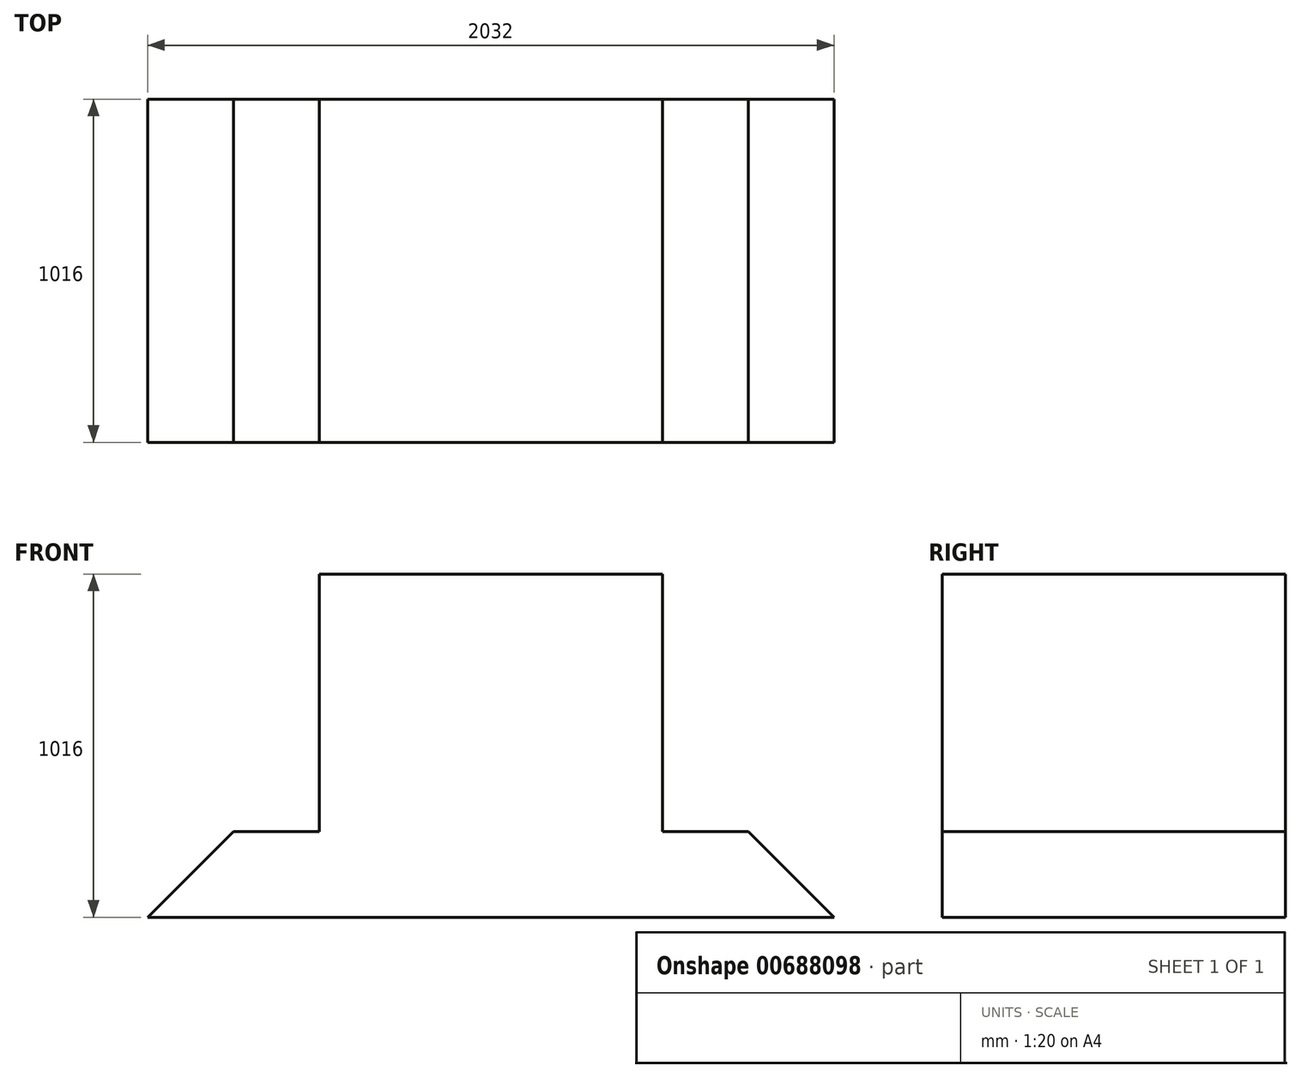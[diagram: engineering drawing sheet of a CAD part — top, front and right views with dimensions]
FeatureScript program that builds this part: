
annotation { "Feature Type Name" : "Feature", "Feature Type Description" : "" }
export const myFeature = defineFeature(function(context is Context, id is Id, definition is map)
    precondition{}
    {
        {
            var Q0;
            Q0=qCreatedBy(makeId("Front.planeOp"),FACE);
            var sketch = newSketch(context, id + "F0", { "sketchPlane" : qUnion([Q0])});
            skLineSegment(sketch, "E0", {"start": v(0, 0) * mm, "end": v(2032, 0) * mm});
            skLineSegment(sketch, "E1", {"start": v(0, 0) * mm, "end": v(254, 254) * mm});
            skLineSegment(sketch, "E2", {"start": v(254, 254) * mm, "end": v(508, 254) * mm});
            skLineSegment(sketch, "E3", {"start": v(508, 254) * mm, "end": v(508, 1016) * mm});
            skLineSegment(sketch, "E4", {"start": v(508, 1016) * mm, "end": v(1524, 1016) * mm});
            skLineSegment(sketch, "E5", {"start": v(1524, 1016) * mm, "end": v(1524, 254) * mm});
            skLineSegment(sketch, "E6", {"start": v(1524, 254) * mm, "end": v(1778, 254) * mm});
            skLineSegment(sketch, "E7", {"start": v(1778, 254) * mm, "end": v(2032, 0) * mm});
            skSolve(sketch);
        }
        {
            var Q0;
            Q0 = qSketchRegion(id + "F0", true);
            extrude(context, id + "F1", {"entities" : qUnion([Q0]), "depth" : 1016 * mm, "offsetDistance" : 25.4 * mm});
        }
    });
